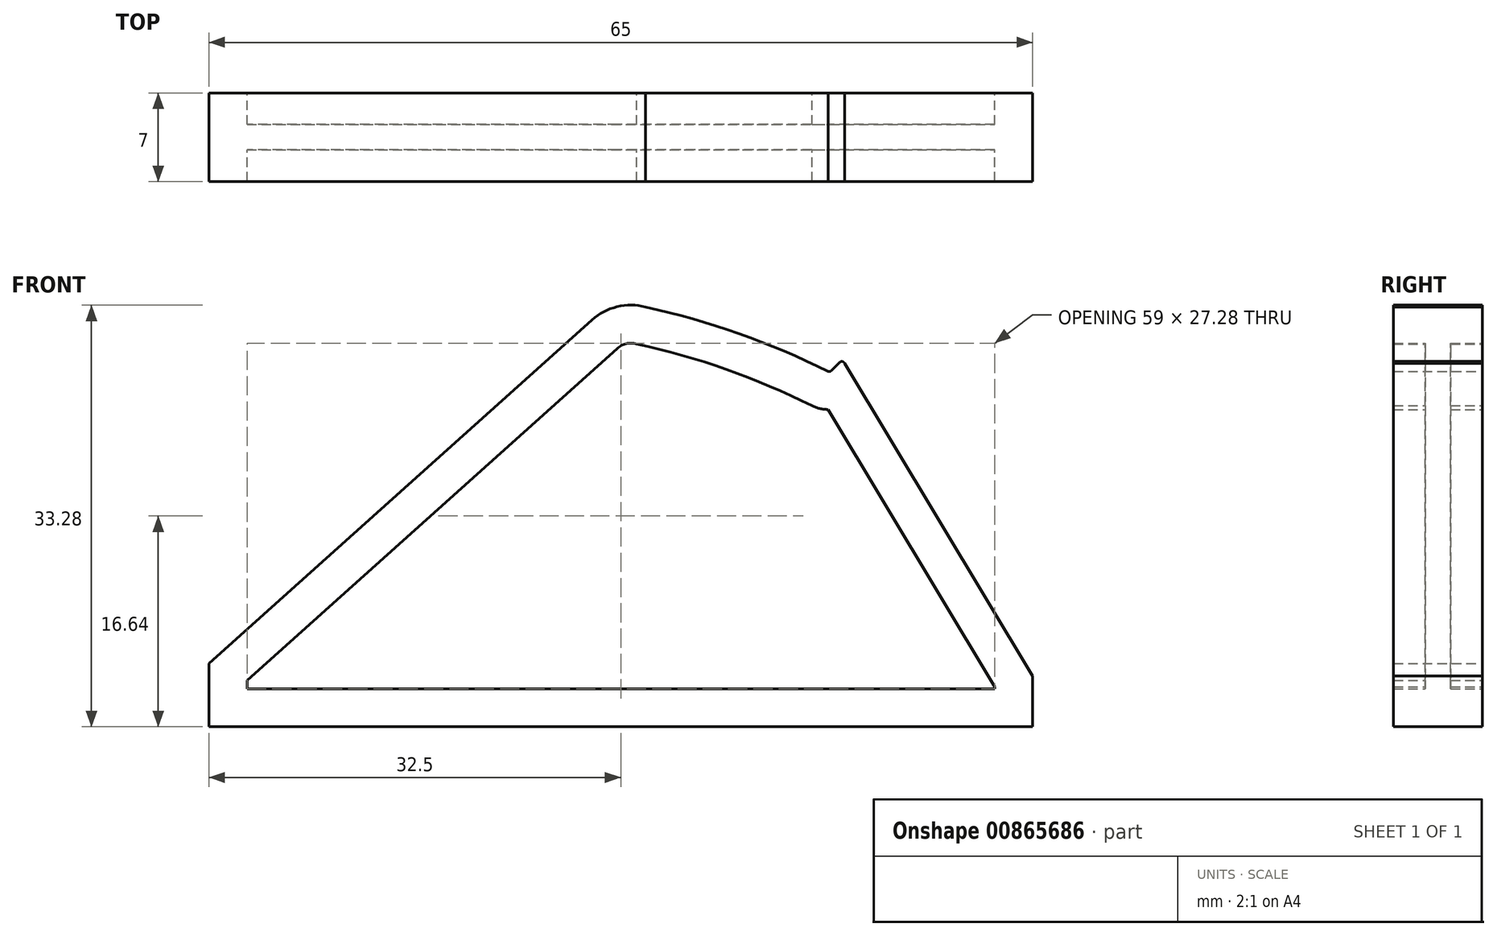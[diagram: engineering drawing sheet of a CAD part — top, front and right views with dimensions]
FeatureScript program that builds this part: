
annotation { "Feature Type Name" : "Feature", "Feature Type Description" : "" }
export const myFeature = defineFeature(function(context is Context, id is Id, definition is map)
    precondition{}
    {
        {
            var Q0;
            Q0=qCreatedBy(makeId("Front.planeOp"),FACE);
            var sketch = newSketch(context, id + "F0", { "sketchPlane" : qUnion([Q0])});
            skLineSegment(sketch, "E0", {"start": v(-32.5, 0) * mm, "end": v(32.5, 0) * mm});
            skLineSegment(sketch, "E1", {"start": v(-0.5, 34) * mm, "end": v(-0.5, -4.24) * mm, "construction": true});
            skLineSegment(sketch, "E2", {"start": v(16.5, 28) * mm, "end": v(16.5, -14.36) * mm, "construction": true});
            skLineSegment(sketch, "E3", {"start": v(-8.9, 34) * mm, "end": v(-33.4, 34) * mm, "construction": true});
            skLineSegment(sketch, "E4", {"start": v(21.76, 28) * mm, "end": v(42.74, 28) * mm, "construction": true});
            skLineSegment(sketch, "E5", {"start": v(17.5, -6.26) * mm, "end": v(17.5, 29) * mm, "construction": true});
            skLineSegment(sketch, "E6", {"start": v(17.5, 29) * mm, "end": v(33, 29) * mm, "construction": true});
            skLineSegment(sketch, "E7", {"start": v(16.61, 28.11) * mm, "end": v(17.26, 28.76) * mm});
            skPoint(sketch, "E8.visualSharp", {"position": v(-0.5, 34) * mm});
            skPoint(sketch, "E9.visualSharp", {"position": v(17.5, 29) * mm});
            skArc(sketch, "E9.filletArc", {"start": v(17.66, 28.7) * mm, "mid": v(17.47, 28.83) * mm, "end": v(17.26, 28.76) * mm});
            skPoint(sketch, "E10.visualSharp", {"position": v(16.5, 28) * mm});
            skArc(sketch, "E10.filletArc", {"start": v(16.35, 28.05) * mm, "mid": v(16.49, 28.04) * mm, "end": v(16.61, 28.11) * mm});
            skLineSegment(sketch, "E11", {"start": v(-32.5, 0) * mm, "end": v(-32.5, 5) * mm});
            skLineSegment(sketch, "E12", {"start": v(-32.5, 5) * mm, "end": v(-2.29, 32.1) * mm});
            skLineSegment(sketch, "E13", {"start": v(32.5, 0) * mm, "end": v(32.5, 4) * mm});
            skLineSegment(sketch, "E14", {"start": v(32.5, 4) * mm, "end": v(17.66, 28.7) * mm});
            skPoint(sketch, "E15", {"position": v(1.96, 33.13) * mm});
            skArc(sketch, "E16", {"start": v(16.35, 28.05) * mm, "mid": v(9.31, 31.04) * mm, "end": v(1.96, 33.13) * mm});
            skArc(sketch, "E17", {"start": v(-2.29, 32.1) * mm, "mid": v(-0.3, 33.15) * mm, "end": v(1.96, 33.13) * mm});
            skSolve(sketch);
        }
        {
            var Q0;
            Q0=makeQuery(id+"F0.imprint","IMPRINT",FACE,{"disambiguationData":[TD([[makeQuery(id+"F0.imprint","IMPRINT",EDGE,{"derivedFrom":sQuery(id+"F0.wireOp",EDGE,"E0")}),1.0]])]});
            var sketch = newSketch(context, id + "F1", { "sketchPlane" : qUnion([Q0])});
            skLineSegment(sketch, "E18.0", {"start": v(29.5, 3.17) * mm, "end": v(16.35, 25.04) * mm});
            skLineSegment(sketch, "E18.1", {"start": v(29.5, 3) * mm, "end": v(29.5, 3.17) * mm});
            skArc(sketch, "E18.2", {"start": v(16.35, 25.04) * mm, "mid": v(15.7, 25.12) * mm, "end": v(15.08, 25.33) * mm});
            skLineSegment(sketch, "E18.3", {"start": v(-29.5, 3) * mm, "end": v(29.5, 3) * mm});
            skArc(sketch, "E18.4", {"start": v(15.08, 25.33) * mm, "mid": v(8.32, 28.2) * mm, "end": v(1.24, 30.22) * mm});
            skArc(sketch, "E18.5", {"start": v(1.24, 30.22) * mm, "mid": v(0.44, 30.24) * mm, "end": v(-0.28, 29.87) * mm});
            skLineSegment(sketch, "E18.6", {"start": v(-0.28, 29.87) * mm, "end": v(-29.5, 3.66) * mm});
            skLineSegment(sketch, "E18.7", {"start": v(-29.5, 3.66) * mm, "end": v(-29.5, 3) * mm});
            skSolve(sketch);
        }
        {
            var Q0;
            Q0=makeQuery(id+"F1.imprint","IMPRINT",FACE,{"disambiguationData":[TD([[makeQuery(id+"F1.imprint","IMPRINT",EDGE,{"derivedFrom":sQuery(id+"F1.wireOp",EDGE,"E18.0")}),-1.0]])]});
            extrude(context, id + "F2", {"entities" : qUnion([Q0]), "endBound" : BoundingType.SYMMETRIC, "depth" : 7 * mm, "offsetDistance" : 25 * mm});
        }
        {
            var Q0;
            Q0 = qSketchRegion(id + "F1", true);
            extrude(context, id + "F3", {"entities" : qUnion([Q0]), "operationType" : NewBodyOperationType.ADD, "endBound" : BoundingType.SYMMETRIC, "depth" : 2 * mm, "offsetDistance" : 25 * mm});
        }
    });
